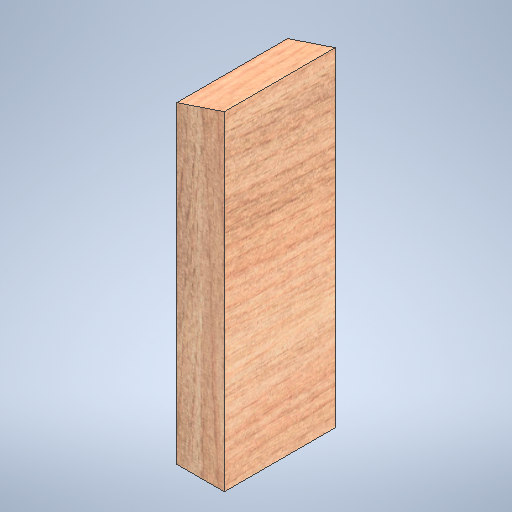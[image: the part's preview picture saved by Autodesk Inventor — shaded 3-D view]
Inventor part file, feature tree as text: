
AUTODESK INVENTOR PART (.ipt)
format: ipt  version: 2025.1 (Build 291241020, 241B)  size: 417,792 bytes
history: native  units: in
note: dims shown in document units (in); Inventor stores cm internally (conversion verified against a paired STEP export)
features: extrude x1, sketch x1
ambient origin geometry x8: Origin, YZ Plane, XZ Plane, XY Plane, X Axis, Y Axis, Z Axis, Center Point
bodies: Solid1 (feature_tree)
feature tree (2):
  extrude  "Extrusion1"  Depth=3.5in TaperAngle=0.0deg
  sketch  "Sketch1"  dims[d2=1.5in d3=3.5in d4=0.0in d5=9.885in d6=10.386in]
